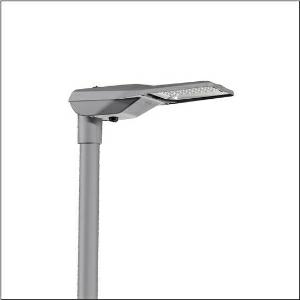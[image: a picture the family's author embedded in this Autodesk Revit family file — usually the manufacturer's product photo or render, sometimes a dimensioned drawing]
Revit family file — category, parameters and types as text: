
# Revit family: streetlight_sl_21_mini___st0_5a_5xe2b43t08hb_0266
name_source: partatom
category: Lighting Fixtures
units: mm (PartAtom-declared; Revit-internal decimal feet)

## family parameters
Cut with Voids When Loaded = No
Host = Face
Light Source = No
Part Type = Normal
Room Calculation Point = No
Round Connector Dimension = Use Diameter
Shared = No

## types (1)
- --- (1 x LED, 9430 lm, 66 W, 4000K)
    Apparent Load = 66 VA
    CIE Flux Codes = 41 75 97 100 100
    Color Rendering = 70
    Color Temperature = 4000K
    Default Elevation = 1800 mm
    Description = Streetlight SL 21 mini, mast luminaire, primary light control with lens, of PMMA, primary optical cover: cover, of toughened safety glass, transparent, light distribution: ST0.5a, light emission: direct distribution, primary light characteristic: asymmetric, installation type: side-entry, post-top, LED, High Power LED, rated luminous flux: 9.430lm, luminous efficacy: 143lm/W, light colour: 740, colour temperature: 4000K, control gear: D4i, control: overheat protection, constant luminous flux control, time-dependent luminous flux control, flexible luminous flux parameterisation, pre-setting: logarithmic dimming characteristic, mains connection: 220..240V, AC, 50/60Hz, start of lifetime: 66W, end of service life: 69W, reduction: 30W, luminaire housing, of diecast aluminium, powder-coated, Siteco® metallic grey (DB 702S), corrosivity category C5 mid according to DIN EN ISO 12944, please order mast flange separately, inclination adjustable: 0°, 5°, 10°, 15°, sealing non-destructively replaceable, multi-level sealing system, length: 628mm, width: 235mm, height: 110mm, mast flange for spigot size: 42mm (side-entry): 5XC10008XM4, 60/48mm (side-entry/post-top): 5XC10108XM2, 76/60mm (side-entry/post-top): 5XC10108XM1, mounting height: 4..8m, Smart Interface below and above, protection rating (complete): IP66, insulation class (complete): insulation class II (safety insulation), certification: CE, ENEC, ENEC+, VDE, impact resistance: IK10, permissible operating ambient temperature for outdoor applications: -40..+50°C, standard-compliant lighting for roads and squares, packaging unit: 1 piece

Light Distribution: ST0.5a
    Height = 110 mm
    Lamp = 1 x LED
    Lamp Light Flux = 9430 lm
    Lamp Power = 66 W
    Lamp count = 1
    Length = 625 mm
    Luminous efficacy = 143 lm/W
    Manufacturer = Siteco
    ModVariant = No
    Model = 5XE2B43T08HB
    Number of Poles = 1
    OnlyDefault = Yes
    Power Factor = 1
    Product Name = Streetlight SL 21 mini | ST0.5a
    Product group = mast luminaire | pylon top
    ProductGroupID = 6100
    Protection Class = Protection class II
    Protection Degree = IP 66
    RLX_Detail_Level = 1
    RLX_Emergency_Light_Flux = 0 lm
    RLX_Emergency_Type = 0
    RLX_Emergency_Type_DB = No
    RlxData = <blob elided: 37265 chars, md5=6f941ade>
    Socket = socket
    Standby Power = 0 W
    System Light Flux = 9430 lm
    System Power = 66 W
    Type Comments = factory setting: luminous flux: 100 % | dim-lin: 254 | 670 mA
    Type Image = l_1003514.jpg
    URL = http://relux.com
    VarID = @adj_212303
    Voltage = 0 V
    Weight = 0.00 kg
    Width = 234 mm

## geometry (parser evidence)
native form markers: Blend x4, Sweep x10
no freeform markers — native parametric forms only
